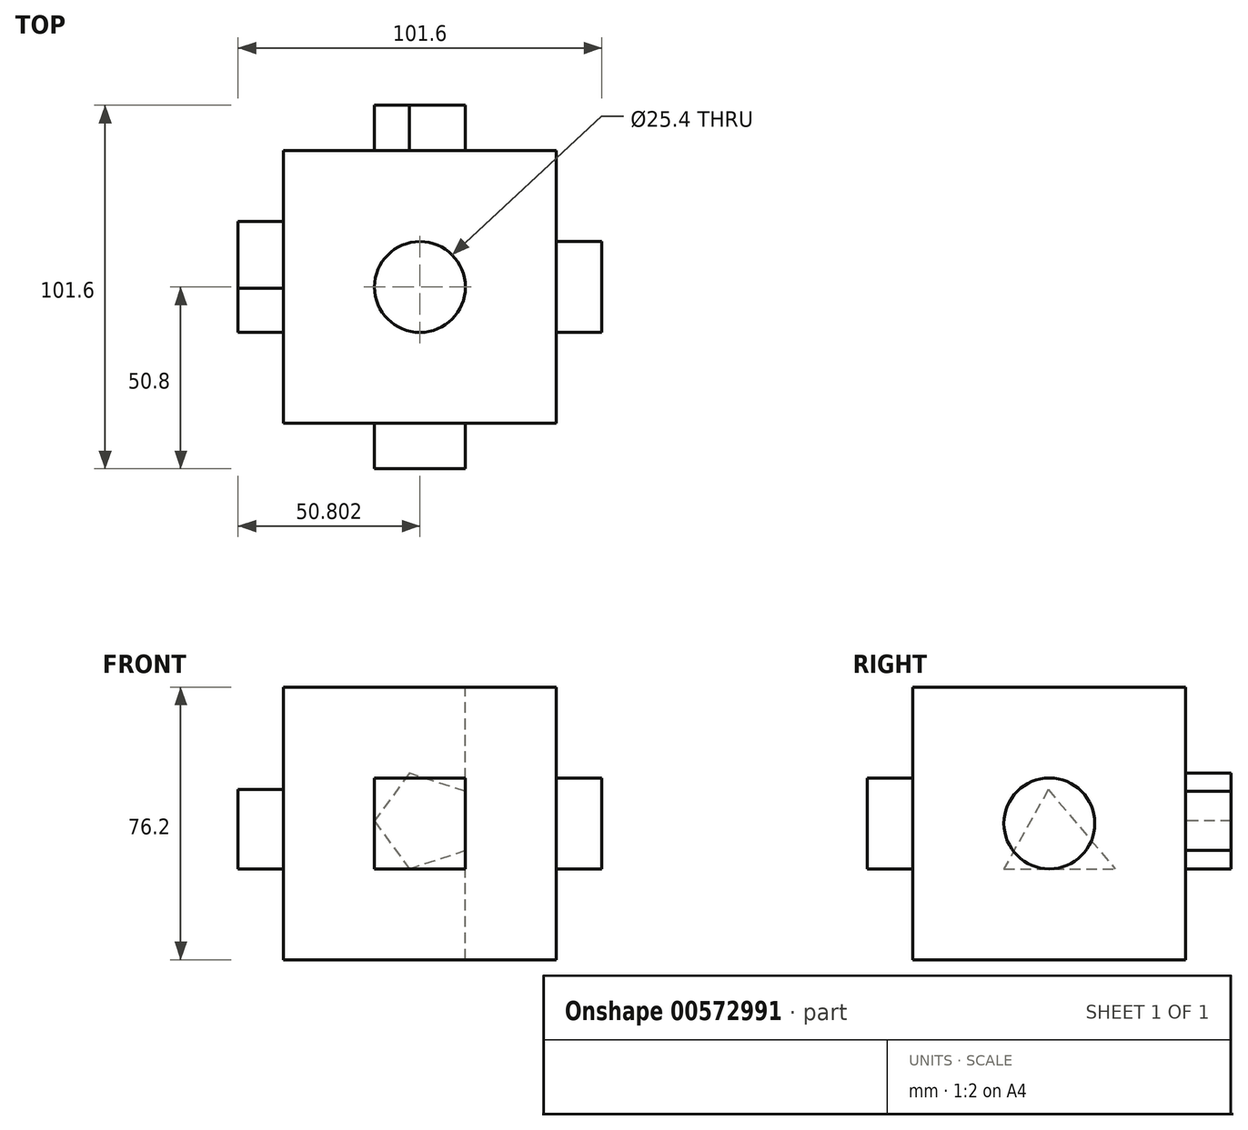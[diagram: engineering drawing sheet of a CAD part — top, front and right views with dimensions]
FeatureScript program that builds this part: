
annotation { "Feature Type Name" : "Feature", "Feature Type Description" : "" }
export const myFeature = defineFeature(function(context is Context, id is Id, definition is map)
    precondition{}
    {
        {
            var Q0;
            Q0=qCreatedBy(makeId("Front.planeOp"),FACE);
            var sketch = newSketch(context, id + "F0", { "sketchPlane" : qUnion([Q0])});
            skLineSegment(sketch, "E0.bottom", {"start": v(30.23, -56.9) * mm, "end": v(-45.97, -56.9) * mm});
            skLineSegment(sketch, "E0.top", {"start": v(30.23, 19.3) * mm, "end": v(-45.97, 19.3) * mm});
            skLineSegment(sketch, "E0.left", {"start": v(30.23, -56.9) * mm, "end": v(30.23, 19.3) * mm});
            skLineSegment(sketch, "E0.right", {"start": v(-45.97, -56.9) * mm, "end": v(-45.97, 19.3) * mm});
            skSolve(sketch);
        }
        {
            var Q0;
            Q0=makeQuery(id+"F0.imprint","IMPRINT",FACE,{"disambiguationData":[TD([[makeQuery(id+"F0.imprint","IMPRINT",EDGE,{"derivedFrom":sQuery(id+"F0.wireOp",EDGE,"E0.bottom")}),-1.0]])]});
            extrude(context, id + "F1", {"entities" : qUnion([Q0]), "oppositeDirection" : true, "depth" : 76.2 * mm, "offsetDistance" : 25.4 * mm});
        }
        {
            var Q0;
            Q0=makeQuery(id+"F1.opExtrude","CAP_FACE",FACE,{"disambiguationData":[OSD([sQuery(id+"F0.wireOp",EDGE,"E0.bottom"),sQuery(id+"F0.wireOp",EDGE,"E0.top"),sQuery(id+"F0.wireOp",EDGE,"E0.left"),sQuery(id+"F0.wireOp",EDGE,"E0.right")])],"isStart":true});
            var sketch = newSketch(context, id + "F2", { "sketchPlane" : qUnion([Q0])});
            skLineSegment(sketch, "E1.bottom", {"start": v(-20.57, -6.1) * mm, "end": v(4.83, -6.1) * mm});
            skLineSegment(sketch, "E1.top", {"start": v(-20.57, -31.5) * mm, "end": v(4.83, -31.5) * mm});
            skLineSegment(sketch, "E1.left", {"start": v(-20.57, -6.1) * mm, "end": v(-20.57, -31.5) * mm});
            skLineSegment(sketch, "E1.right", {"start": v(4.83, -6.1) * mm, "end": v(4.83, -31.5) * mm});
            skSolve(sketch);
        }
        {
            var Q0;
            Q0=makeQuery(id+"F2.imprint","IMPRINT",FACE,{"disambiguationData":[TD([[makeQuery(id+"F2.imprint","IMPRINT",EDGE,{"derivedFrom":sQuery(id+"F2.wireOp",EDGE,"E1.bottom")}),-1.0]])]});
            extrude(context, id + "F3", {"entities" : qUnion([Q0]), "operationType" : NewBodyOperationType.ADD, "depth" : 12.7 * mm, "offsetDistance" : 25.4 * mm});
        }
        {
            var Q0;
            Q0=makeQuery(id+"F1.opExtrude","SWEPT_FACE",FACE,{"disambiguationData":[OSD([sQuery(id+"F0.wireOp",EDGE,"E0.left")])]});
            var sketch = newSketch(context, id + "F4", { "sketchPlane" : qUnion([Q0])});
            skCircle(sketch, "E2", {"center": v(38.1, -18.8) * mm, "radius": 12.7 * mm});
            skSolve(sketch);
        }
        {
            var Q0;
            Q0=makeQuery(id+"F4.imprint","IMPRINT",FACE,{"disambiguationData":[TD([[makeQuery(id+"F4.imprint","IMPRINT",EDGE,{"derivedFrom":sQuery(id+"F4.wireOp",EDGE,"E2")}),1.0]])]});
            extrude(context, id + "F5", {"entities" : qUnion([Q0]), "operationType" : NewBodyOperationType.ADD, "depth" : 12.7 * mm, "offsetDistance" : 25.4 * mm});
        }
        {
            var Q0;
            Q0=makeQuery(id+"F1.opExtrude","SWEPT_FACE",FACE,{"disambiguationData":[OSD([sQuery(id+"F0.wireOp",EDGE,"E0.top")])]});
            var sketch = newSketch(context, id + "F6", { "sketchPlane" : qUnion([Q0])});
            skPoint(sketch, "E3", {"position": v(-7.87, 38.1) * mm});
            skSolve(sketch);
        }
        {
            var Q0;
            Q0=sQuery(id+"F6.wireOp",VERTEX,"E3");
            var Q1;
            Q1=makeQuery(id+"F1.opExtrude","SWEPT_BODY",BODY,{"disambiguationData":[OSD([sQuery(id+"F0.wireOp",EDGE,"E0.bottom"),sQuery(id+"F0.wireOp",EDGE,"E0.top"),sQuery(id+"F0.wireOp",EDGE,"E0.left"),sQuery(id+"F0.wireOp",EDGE,"E0.right")])]});
            hole(context, id + "F7", {"style" : HoleStyle.SIMPLE, "endStyle" : HoleEndStyle.THROUGH, "holeDiameter" : 25.4 * mm, "isTappedThrough" : true, "tappedDepth" : 12.7 * mm, "tapClearance" : 3, "locations" : qUnion([Q0]), "scope" : qUnion([Q1])});
        }
        {
            var Q0;
            Q0=makeQuery(id+"F1.opExtrude","SWEPT_FACE",FACE,{"disambiguationData":[OSD([sQuery(id+"F0.wireOp",EDGE,"E0.right")])]});
            var sketch = newSketch(context, id + "F8", { "sketchPlane" : qUnion([Q0])});
            skLineSegment(sketch, "E4", {"start": v(-37.8, -9.32) * mm, "end": v(-54.15, -28.77) * mm});
            skLineSegment(sketch, "E5", {"start": v(-37.8, -9.32) * mm, "end": v(-25.4, -31.5) * mm});
            skLineSegment(sketch, "E6", {"start": v(-25.4, -31.5) * mm, "end": v(-56.44, -31.5) * mm});
            skLineSegment(sketch, "E7", {"start": v(-54.15, -28.77) * mm, "end": v(-56.44, -31.5) * mm});
            skSolve(sketch);
        }
        {
            var Q0;
            Q0 = qSketchRegion(id + "F8", true);
            extrude(context, id + "F9", {"entities" : qUnion([Q0]), "operationType" : NewBodyOperationType.ADD, "depth" : 12.7 * mm, "offsetDistance" : 25.4 * mm});
        }
        {
            var Q0;
            Q0=makeQuery(id+"F1.opExtrude","CAP_FACE",FACE,{"disambiguationData":[OSD([sQuery(id+"F0.wireOp",EDGE,"E0.bottom"),sQuery(id+"F0.wireOp",EDGE,"E0.top"),sQuery(id+"F0.wireOp",EDGE,"E0.left"),sQuery(id+"F0.wireOp",EDGE,"E0.right")])],"isStart":false});
            var sketch = newSketch(context, id + "F10", { "sketchPlane" : qUnion([Q0])});
            skCircle(sketch, "E8.cCircle", {"center": v(6.53, -18.14) * mm, "radius": 11.36 * mm, "construction": true});
            skLineSegment(sketch, "E8.0", {"start": v(-4.83, -26.39) * mm, "end": v(-4.83, -9.88) * mm});
            skLineSegment(sketch, "E8.1", {"start": v(-4.83, -9.88) * mm, "end": v(10.87, -4.78) * mm});
            skLineSegment(sketch, "E8.2", {"start": v(10.87, -4.78) * mm, "end": v(20.57, -18.14) * mm});
            skLineSegment(sketch, "E8.3", {"start": v(20.57, -18.14) * mm, "end": v(10.87, -31.5) * mm});
            skLineSegment(sketch, "E8.4", {"start": v(10.87, -31.5) * mm, "end": v(-4.83, -26.39) * mm});
            skPoint(sketch, "E8.0.midPoint", {"position": v(-4.83, -18.14) * mm});
            skSolve(sketch);
        }
        {
            var Q0;
            Q0 = qSketchRegion(id + "F10", true);
            extrude(context, id + "F11", {"entities" : qUnion([Q0]), "operationType" : NewBodyOperationType.ADD, "depth" : 12.7 * mm, "offsetDistance" : 25.4 * mm});
        }
    });
